# Revit family: pcfy-rp80_140hmg9_60hz
name_source: partatom
category: 機械設備
units: mm (PartAtom-declared; Revit-internal decimal feet)

## family parameters
OmniClass タイトル = Split System Air Conditioning Units
OmniClass 番号 = 23.75.10.24.21.27.27
パーツ タイプ = 標準
ロード時にボイドで切り取り = いいえ
丸型コネクタ寸法 = 直径を使用
作業面ベース = いいえ
共有 = いいえ
常に垂直 = はい
部屋計算ポイント = はい

## types (2) — shared parameters
Clearance Back = 0 mm
Clearance Bottom = 500 mm
Clearance Front = 1500 mm
Clearance Left = 100 mm
Clearance Right = 100 mm
Clearance Top = 2 mm
Depth = 650 mm
Height = 280 mm
IfcExportAs = IfcUnitaryEquipmentType
IfcExportType = AIRCONDITIONINGUNIT
OmniClassCode = 23-33 17 13 11
S_H = 295 mm
URL = https://www.mitsubishielectric.co.jp
Uniclass2015Code = Pr_70_65_03_84
Uniclass2015Title = Split coil remote air cooled condensing units
Uniclass2015Version = Systems v1.9
ケーブルサイズ = 2 mm
サービススペース = はい
ドレン管径 = 25.00 mm
ドレン管径 (外径) = 32 mm
ドレン管高さ = 254 mm
パネルマテリアル = <カテゴリ別>
仕様書バージョン = Version1.0
企業コード = 108420
冷媒ガス管位置 = 197 mm
冷媒ガス管径 = 15.88 mm
冷媒ガス管高さ = 165 mm
冷媒液管位置 = 174 mm
冷媒液管径 = 9.52 mm
冷媒液管高さ = 165 mm
冷媒管径 = 100.00 mm
冷媒管径符号 = Bd
冷媒高低圧ガス管径 = 0.00 mm
分類コード = 50053003221080
加湿給水管径 = 0.00 mm
参照している仕様書等のバージョン = 公共建築工事標準仕様書（機械設備工事編）平成31年度版
吊りボルト_H = 43 mm
吊り位置Y = 320 mm
周波数 = 60 Hz
呼称 = 室内機_厨房用天井吊（露出）形
始動方式 = 直入
形式 = 厨房用天井吊（露出）形
推奨ブレーカー容量 = 15 A
本体マテリアル = <カテゴリ別>
極数 = 1
法定耐用年数 = 6
発停方法 = 付属スイッチ
相 = 1
積算_科目 = 1 空気調和設備
符号 = ACP_CRK
製品リリース年月 = 2022/9/15
製品出荷対象 = 国内
製造元 = 三菱電機株式会社
設置方法 = 天井吊形
設計冷房能力 = 0 kW
設計冷房能力_顕熱 = 0 kW
設計暖房能力 = 0.00 kW
説明 = ビル用マルチ 天吊形室内機(厨房用)
負荷分類 = 3_ファン類
運転質量 = 0.00 kg
電圧 = 200 V
電源_H = 0 mm
zero-valued in all types: 価格, 有効加湿量

## per-type parameters (varying)
| type | Line | MAX風量 | MIN風量 | Width | 冷房能力 | 吊り位置X | 暖房能力 | 構成品番 | 消費電力 | 消費電力_冷房 | 消費電力_暖房 | 製品質量 | 質量 | 電動機出力_送風機 | 音響パワーレベル(dB) | 音響パワーレベル（弱）(dB) | 風量 | 風量_弱 (m3/min) | 風量_強 (m3/min) |
| 厨房天吊_PCFY-P80HMG9 | いいえ | 1140.0 m³/h | 840.0 m³/h | 1136 mm | 8 kW | 1180 mm | 9.00 kW | PCFY-P80HMG9 | 0.13 kW | 0.13 kW | 0.13 kW | 41.00 kg | 49.20 kg | 0.04 kW | 57 | 54 | 1140.0 m³/h | 14 | 19 |
| 厨房天吊_PCFY-P140HMG9 | はい | 2280.0 m³/h | 1680.0 m³/h | 1520 mm | 14 kW | 1564 mm | 16.00 kW | PCFY-P140HMG9 | 0.30 kW | 0.30 kW | 0.30 kW | 56.00 kg | 67.20 kg | 0.16 kW | 68 | 61 | 2280.0 m³/h | 28 | 38 |

## geometry (parser evidence)
native form markers: Sweep x3
no freeform markers — native parametric forms only
